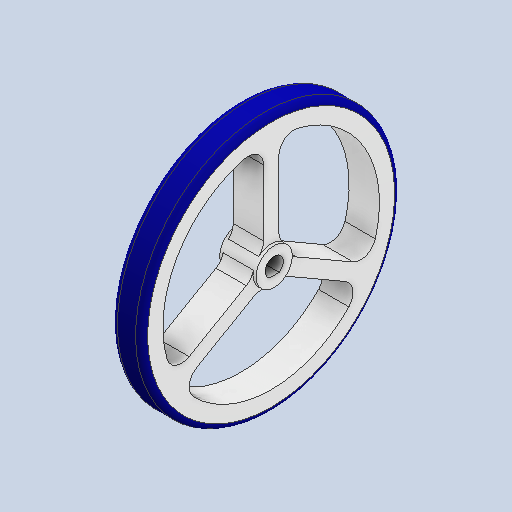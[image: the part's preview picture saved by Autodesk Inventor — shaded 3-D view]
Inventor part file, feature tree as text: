
AUTODESK INVENTOR PART (.ipt)
format: ipt  version: 2022.3 (Build 263350030, 350C)  size: 216,576 bytes
history: native  units: mm
features: extrude x4, sketch x4, fillet x2, projected_geometry x1
ambient origin geometry x8: Origin, YZ Plane, XZ Plane, XY Plane, X Axis, Y Axis, Z Axis, Center Point
bodies: Solid1 (feature_tree)
feature tree (11):
  extrude  "Extrusion1"  Depth=10.0mm TaperAngle=0.0deg
  fillet  "Fillet1"  Radius=2.0mm
  extrude  "Extrusion2"  Depth=12.0mm TaperAngle=0.0deg
  extrude  "Extrusion3"  Depth=3.0mm
  extrude  "Extrusion4"  Depth=5.0mm
  fillet  "Fillet2"  Radius=5.0mm
  sketch  "Sketch1"  dims[d0=85.5mm d1=10.0mm d2=0.0mm d3=2.0mm]
  sketch  "Sketch2"  dims[d9=12.0mm d10=12.0mm d11=0.0mm]
  sketch  "Sketch3"  dims[d12=3.0mm d13=2.5mm]
  sketch  "Sketch4"  dims[d14=0.0mm d15=0.0mm d17=71.5mm d18=5.0mm d19=30.0mm d21=360.0deg d23=0.0mm d24=0.0mm d25=5.0mm]
  projected_geometry  "Project Cut Edges1"
